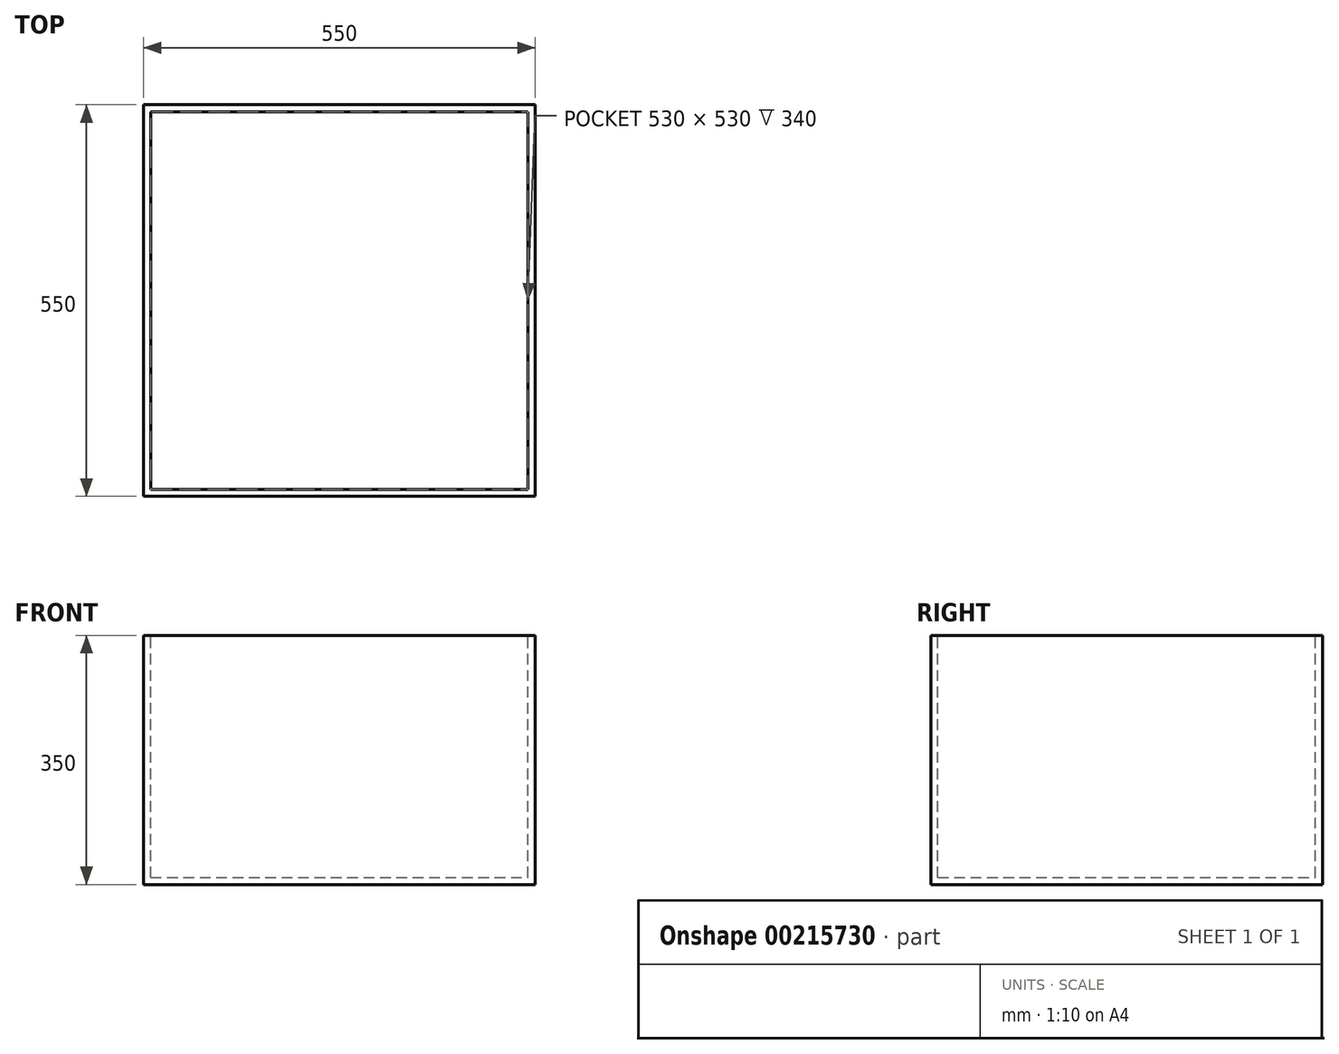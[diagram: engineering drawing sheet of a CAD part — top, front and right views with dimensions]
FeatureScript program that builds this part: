
annotation { "Feature Type Name" : "Feature", "Feature Type Description" : "" }
export const myFeature = defineFeature(function(context is Context, id is Id, definition is map)
    precondition{}
    {
        {
            var Q0;
            Q0=qCreatedBy(makeId("Top.planeOp"),FACE);
            var sketch = newSketch(context, id + "F0", { "sketchPlane" : qUnion([Q0])});
            skLineSegment(sketch, "E0.bottom", {"start": v(0, 0) * mm, "end": v(550, 0) * mm});
            skLineSegment(sketch, "E0.top", {"start": v(0, 550) * mm, "end": v(550, 550) * mm});
            skLineSegment(sketch, "E0.left", {"start": v(0, 0) * mm, "end": v(0, 550) * mm});
            skLineSegment(sketch, "E0.right", {"start": v(550, 0) * mm, "end": v(550, 550) * mm});
            skSolve(sketch);
        }
        {
            var Q0;
            Q0=qSketchRegion(id+"F0",true);
            extrude(context, id + "F1", {"entities" : qUnion([Q0]), "oppositeDirection" : true, "depth" : 350 * mm});
        }
        {
            var Q0;
            Q0=qCreatedBy(makeId("Top.planeOp"),FACE);
            var sketch = newSketch(context, id + "F2", { "sketchPlane" : qUnion([Q0])});
            skLineSegment(sketch, "E1.bottom", {"start": v(10, 10) * mm, "end": v(540, 10) * mm});
            skLineSegment(sketch, "E1.top", {"start": v(10, 540) * mm, "end": v(540, 540) * mm});
            skLineSegment(sketch, "E1.left", {"start": v(10, 10) * mm, "end": v(10, 540) * mm});
            skLineSegment(sketch, "E1.right", {"start": v(540, 10) * mm, "end": v(540, 540) * mm});
            skSolve(sketch);
        }
        {
            var Q0;
            Q0=qSketchRegion(id+"F2",true);
            extrude(context, id + "F3", {"entities" : qUnion([Q0]), "operationType" : NewBodyOperationType.REMOVE, "oppositeDirection" : true, "depth" : 340 * mm});
        }
    });
